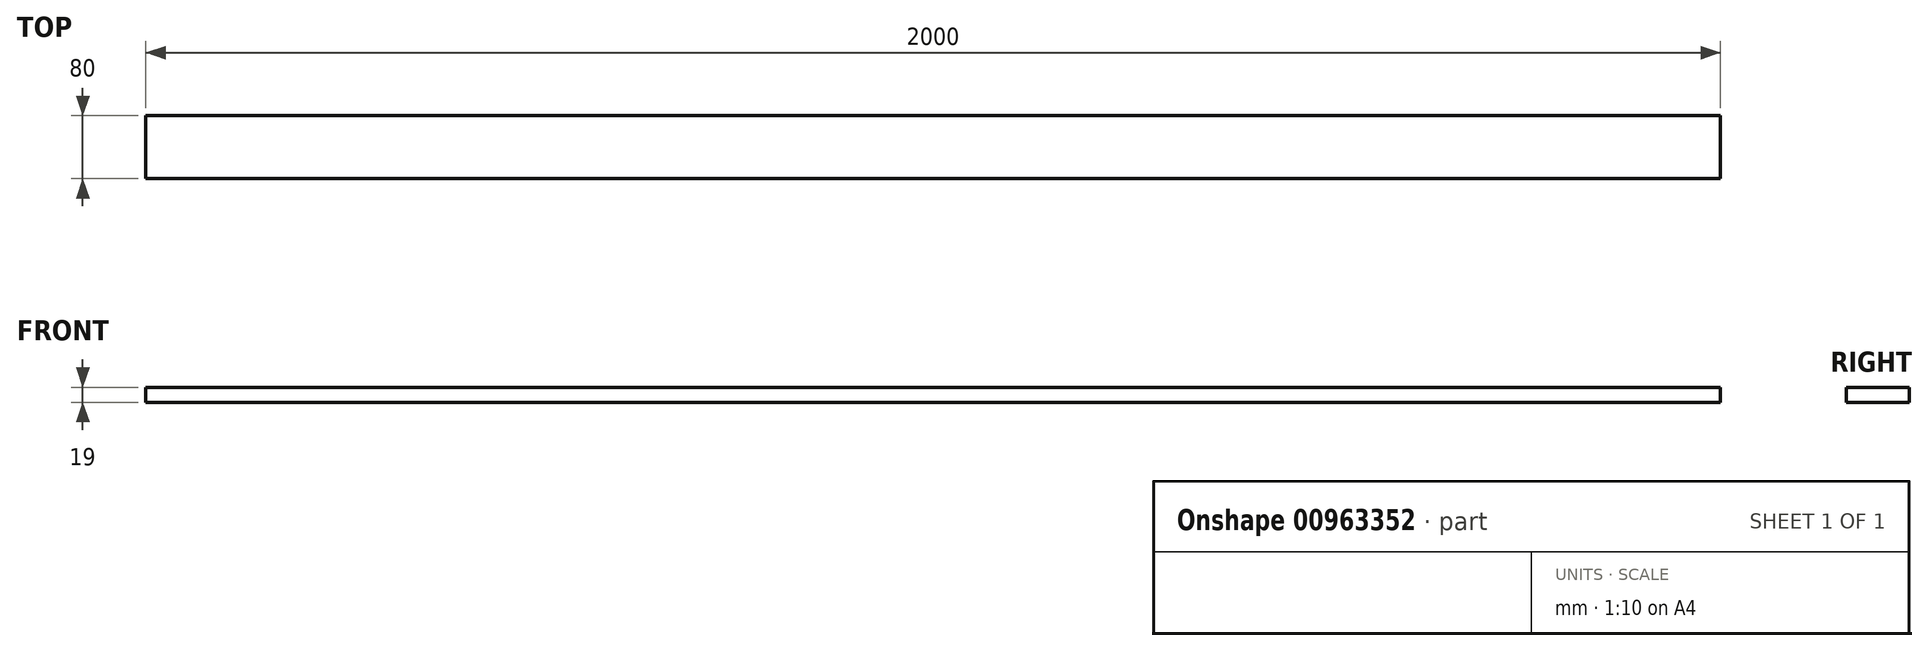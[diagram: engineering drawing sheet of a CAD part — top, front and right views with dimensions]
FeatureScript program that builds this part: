
annotation { "Feature Type Name" : "Feature", "Feature Type Description" : "" }
export const myFeature = defineFeature(function(context is Context, id is Id, definition is map)
    precondition{}
    {
        {
            var Q0;
            Q0=qCreatedBy(makeId("Top.planeOp"),FACE);
            var sketch = newSketch(context, id + "F0", { "sketchPlane" : qUnion([Q0])});
            skLineSegment(sketch, "E0.bottom", {"start": v(1000, -40) * mm, "end": v(-1000, -40) * mm});
            skLineSegment(sketch, "E0.top", {"start": v(1000, 40) * mm, "end": v(-1000, 40) * mm});
            skLineSegment(sketch, "E0.left", {"start": v(1000, -40) * mm, "end": v(1000, 40) * mm});
            skLineSegment(sketch, "E0.right", {"start": v(-1000, -40) * mm, "end": v(-1000, 40) * mm});
            skPoint(sketch, "E0.middle", {"position": v(0, 0) * mm});
            skSolve(sketch);
        }
        {
            var Q0;
            Q0 = qSketchRegion(id + "F0", true);
            extrude(context, id + "F1", {"entities" : qUnion([Q0]), "depth" : 19 * mm, "offsetDistance" : 25 * mm});
        }
    });
